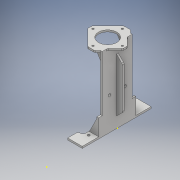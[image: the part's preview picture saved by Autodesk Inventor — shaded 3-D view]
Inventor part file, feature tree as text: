
AUTODESK INVENTOR PART (.ipt)
format: ipt  version: 2018 (Build 220112000, 112)  size: 371,712 bytes
history: native  units: mm
features: sketch x20, extrude x17, reference x12, other x4, fillet x3, plane x2, mirror x2, chamfer x1
ambient origin geometry x8: Origin, YZ Plane, XZ Plane, XY Plane, X Axis, Y Axis, Z Axis, Center Point
bodies: Solid1 (feature_tree)
feature tree (61):
  extrude  "Extrusion1"  Depth=13.0mm
  fillet  "Fillet1"  Radius=30.0mm
  extrude  "Extrusion2"  Depth=55.0mm
  extrude  "Extrusion3"  Depth=16.0mm
  extrude  "Extrusion4"  Depth=7.0mm
  extrude  "Extrusion5"  Depth=6.0mm
  chamfer  "Chamfer1"  Distance=241.0mm
  fillet  "Fillet2"  Radius=6.0mm
  extrude  "Extrusion6"  Depth=10.0mm
  plane  "Work Plane1"
  plane  "Work Plane2"
  sketch  "Sketch8"  dims[d18=10.0mm d19=4.0mm]
  extrude  "Extrusion8"  Depth=4.0mm
  mirror  "Mirror1"
  extrude  "Extrusion9"  Depth=7.0mm TaperAngle=0.0deg
  mirror  "Mirror2"
  sketch  "Sketch11"  dims[d29=13.0mm d30=2.0mm d31=45.0deg d32=7.0mm]
  extrude  "Extrusion10"  Depth=26.0mm
  fillet  "Fillet3"  Radius=26.0mm
  sketch  "Sketch13"  dims[d38=-10.0mm d39=25.0mm]
  sketch  "Sketch14"  dims[d40=50.0mm d41=6.0mm d42=0.0mm]
  sketch  "Sketch15"  dims[d43=30.0mm d45=50.0mm]
  extrude  "Extrusion11"  Depth=7.0mm
  extrude  "Extrusion12"  Depth=7.0mm TaperAngle=0.0deg
  extrude  "Extrusion13"  Depth=25.0mm
  extrude  "Extrusion14"  Depth=6.0mm TaperAngle=0.0deg
  extrude  "Extrusion15"  Depth=30.0mm
  extrude  "Extrusion16"  Depth=90.0mm
  extrude  "Extrusion19"  TaperAngle=90.0deg  [1 undecoded]
  extrude  "Extrusion20"  Depth=20.0mm
  sketch  "Sketch1"  dims[d0=230.0mm d1=13.0mm d2=30.0mm]
  reference  "Reference1"
  sketch  "Sketch2"  dims[d3=55.0mm d4=55.0mm]
  reference  "Reference2"
  reference  "Reference3"
  sketch  "Sketch3"  dims[d5=55.0mm d6=16.0mm]
  sketch  "Sketch4"  dims[d7=6.0mm d8=0.0mm d9=7.0mm]
  reference  "Reference4"
  reference  "Reference5"
  reference  "Reference6"
  reference  "Reference7"
  sketch  "Sketch5"  dims[d10=100.0mm d11=6.0mm d12=241.0mm d13=0.0mm d14=6.0mm]
  sketch  "Sketch6"  dims[d15=85.0mm d16=0.0mm d17=10.0mm]
  reference  "Reference8"
  reference  "Reference9"
  reference  "Reference10"
  reference  "Reference11"
  reference  "Reference12"
  sketch  "Sketch9"  dims[d20=4.0mm d23=7.0mm d24=0.0mm]
  sketch  "Sketch10"  dims[d25=6.0mm d26=40.0mm d27=26.0mm d28=0.0mm]
  sketch  "Sketch12"  dims[d33=0.5mm d34=7.0mm d35=0.0mm]
  sketch  "Sketch16"  dims[d46=6.0mm d47=0.0mm d48=90.0mm]
  sketch  "Sketch17"  dims[d49=90.0mm d50=90.0deg]
  sketch  "Sketch18"  dims[d51=45.0deg d52=20.0mm]
  sketch  "Sketch19"  dims[d53=6.0mm d54=0.0mm]
  sketch  "Sketch20"  dims[d55=7.0mm]
  sketch  "Sketch23"  dims[d56=42.0mm d57=24.5mm d58=7.0mm d59=74.0mm d60=21.5mm d61=8.0mm d62=42.0mm d63=74.0mm d64=7.0mm d65=8.0mm d66=55.0mm d67=12.0mm d68=0.0mm d69=55.0mm d70=12.0mm d71=0.0mm d73=16.0mm d74=0.0mm d75=16.0mm d76=0.0mm d77=16.0mm d78=0.0mm d79=16.0mm d80=0.0mm d85=16.0mm d86=0.0mm d87=9.0mm d88=24.0mm d89=102.38mm d90=9.0mm d91=102.38mm d92=24.0mm d93=10.0mm d94=0.0mm]
  other  "Lathe Model 2018.iam"
  other  "saddle:1"
  other  "Servo Motor:2"
  other  "Body:1"
note: 1 required parameter value undecoded (feature->parameter linkage not recoverable at this tier; creation-order binding heuristic only, values carry confidence <= 0.55)
